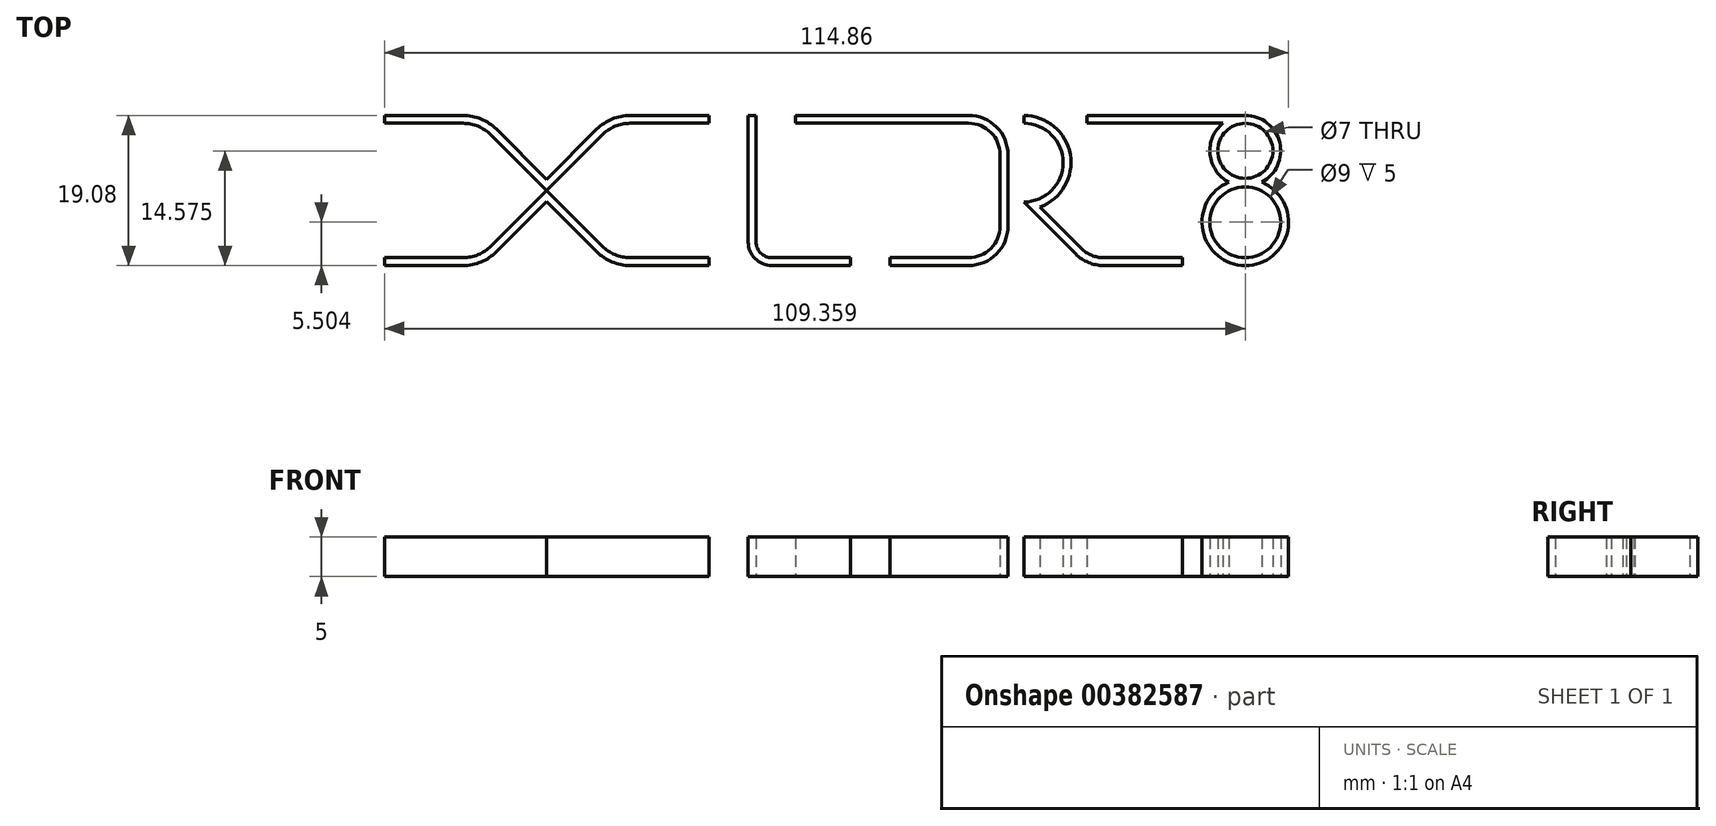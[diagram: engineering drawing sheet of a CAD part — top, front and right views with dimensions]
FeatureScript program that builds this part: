
annotation { "Feature Type Name" : "Feature", "Feature Type Description" : "" }
export const myFeature = defineFeature(function(context is Context, id is Id, definition is map)
    precondition{}
    {
        {
            var Q0;
            Q0=qCreatedBy(makeId("Top.planeOp"),FACE);
            var sketch = newSketch(context, id + "F0", { "sketchPlane" : qUnion([Q0])});
            skLineSegment(sketch, "E0", {"start": v(0, 0) * mm, "end": v(7.07, -7.07) * mm});
            skLineSegment(sketch, "E1", {"start": v(0, 0) * mm, "end": v(-7.07, 7.07) * mm});
            skLineSegment(sketch, "E2", {"start": v(0, 0) * mm, "end": v(7.07, 7.07) * mm});
            skLineSegment(sketch, "E3", {"start": v(0, 0) * mm, "end": v(-7.07, -7.07) * mm});
            skArc(sketch, "E4", {"start": v(10.6, 8.54) * mm, "mid": v(8.7, 8.15) * mm, "end": v(7.07, 7.07) * mm});
            skArc(sketch, "E5", {"start": v(-7.07, 7.07) * mm, "mid": v(-8.7, 8.15) * mm, "end": v(-10.6, 8.54) * mm});
            skArc(sketch, "E6", {"start": v(-10.6, -8.54) * mm, "mid": v(-8.7, -8.15) * mm, "end": v(-7.07, -7.07) * mm});
            skArc(sketch, "E7", {"start": v(7.07, -7.07) * mm, "mid": v(8.7, -8.15) * mm, "end": v(10.6, -8.54) * mm});
            skLineSegment(sketch, "E8", {"start": v(10.6, 8.54) * mm, "end": v(20.6, 8.54) * mm});
            skLineSegment(sketch, "E9", {"start": v(-10.6, 8.54) * mm, "end": v(-20.6, 8.54) * mm});
            skLineSegment(sketch, "E10", {"start": v(10.6, -8.54) * mm, "end": v(20.6, -8.54) * mm});
            skLineSegment(sketch, "E11", {"start": v(-10.6, -8.54) * mm, "end": v(-20.6, -8.54) * mm});
            skLineSegment(sketch, "E12.0", {"start": v(-10.6, 9.54) * mm, "end": v(-20.6, 9.54) * mm});
            skArc(sketch, "E12.1", {"start": v(-6.36, 7.78) * mm, "mid": v(-8.31, 9.08) * mm, "end": v(-10.6, 9.54) * mm});
            skLineSegment(sketch, "E12.2", {"start": v(10.6, 9.54) * mm, "end": v(20.6, 9.54) * mm});
            skArc(sketch, "E12.3", {"start": v(10.6, 9.54) * mm, "mid": v(8.31, 9.08) * mm, "end": v(6.36, 7.78) * mm});
            skLineSegment(sketch, "E12.4", {"start": v(0, 1.41) * mm, "end": v(6.36, 7.78) * mm});
            skLineSegment(sketch, "E12.5", {"start": v(0, 1.41) * mm, "end": v(-6.36, 7.78) * mm});
            skLineSegment(sketch, "E13.0", {"start": v(-10.6, -9.54) * mm, "end": v(-20.6, -9.54) * mm});
            skArc(sketch, "E13.1", {"start": v(-10.6, -9.54) * mm, "mid": v(-8.31, -9.08) * mm, "end": v(-6.36, -7.78) * mm});
            skLineSegment(sketch, "E13.2", {"start": v(10.6, -9.54) * mm, "end": v(20.6, -9.54) * mm});
            skArc(sketch, "E13.3", {"start": v(6.36, -7.78) * mm, "mid": v(8.31, -9.08) * mm, "end": v(10.6, -9.54) * mm});
            skLineSegment(sketch, "E13.4", {"start": v(0, -1.41) * mm, "end": v(6.36, -7.78) * mm});
            skLineSegment(sketch, "E13.5", {"start": v(0, -1.41) * mm, "end": v(-6.36, -7.78) * mm});
            skLineSegment(sketch, "E14", {"start": v(-20.6, 9.54) * mm, "end": v(-20.6, 8.54) * mm});
            skLineSegment(sketch, "E15", {"start": v(-20.6, -9.54) * mm, "end": v(-20.6, -8.54) * mm});
            skLineSegment(sketch, "E16", {"start": v(20.6, -8.54) * mm, "end": v(20.6, -9.54) * mm});
            skLineSegment(sketch, "E17", {"start": v(20.6, 9.54) * mm, "end": v(20.6, 8.54) * mm});
            skLineSegment(sketch, "E18", {"start": v(0, 0) * mm, "end": v(0, 0) * mm});
            skLineSegment(sketch, "E19", {"start": v(25.6, 9.54) * mm, "end": v(25.6, -6.54) * mm});
            skArc(sketch, "E20", {"start": v(25.6, -6.54) * mm, "mid": v(26.49, -8.66) * mm, "end": v(28.6, -9.54) * mm});
            skLineSegment(sketch, "E21", {"start": v(28.6, -9.54) * mm, "end": v(38.6, -9.54) * mm});
            skLineSegment(sketch, "E22.0", {"start": v(28.6, -8.54) * mm, "end": v(38.6, -8.54) * mm});
            skArc(sketch, "E22.1", {"start": v(26.6, -6.54) * mm, "mid": v(27.2, -7.95) * mm, "end": v(28.6, -8.54) * mm});
            skLineSegment(sketch, "E22.2", {"start": v(26.6, 9.54) * mm, "end": v(26.6, -6.54) * mm});
            skLineSegment(sketch, "E23", {"start": v(25.6, 9.54) * mm, "end": v(26.6, 9.54) * mm});
            skLineSegment(sketch, "E24", {"start": v(38.6, -8.54) * mm, "end": v(38.6, -9.54) * mm});
            skLineSegment(sketch, "E25", {"start": v(43.6, -9.54) * mm, "end": v(53.6, -9.54) * mm});
            skArc(sketch, "E26", {"start": v(53.6, -9.54) * mm, "mid": v(57.14, -8.07) * mm, "end": v(58.6, -4.54) * mm});
            skLineSegment(sketch, "E27", {"start": v(58.6, -4.54) * mm, "end": v(58.6, 4.54) * mm});
            skArc(sketch, "E28", {"start": v(58.6, 4.54) * mm, "mid": v(57.14, 8.07) * mm, "end": v(53.6, 9.54) * mm});
            skLineSegment(sketch, "E29", {"start": v(53.6, 9.54) * mm, "end": v(31.6, 9.54) * mm});
            skLineSegment(sketch, "E30.0", {"start": v(53.6, 8.54) * mm, "end": v(31.6, 8.54) * mm});
            skLineSegment(sketch, "E30.1", {"start": v(43.6, -8.54) * mm, "end": v(53.6, -8.54) * mm});
            skArc(sketch, "E30.2", {"start": v(53.6, -8.54) * mm, "mid": v(56.44, -7.36) * mm, "end": v(57.6, -4.54) * mm});
            skLineSegment(sketch, "E30.3", {"start": v(57.6, -4.54) * mm, "end": v(57.6, 4.54) * mm});
            skArc(sketch, "E30.4", {"start": v(57.6, 4.54) * mm, "mid": v(56.44, 7.36) * mm, "end": v(53.6, 8.54) * mm});
            skLineSegment(sketch, "E31", {"start": v(31.6, 8.54) * mm, "end": v(31.6, 9.54) * mm});
            skLineSegment(sketch, "E32", {"start": v(43.6, -8.54) * mm, "end": v(43.6, -9.54) * mm});
            skLineSegment(sketch, "E33", {"start": v(60.6, -1.46) * mm, "end": v(67.21, -8.07) * mm});
            skArc(sketch, "E34", {"start": v(67.21, -8.07) * mm, "mid": v(68.84, -9.15) * mm, "end": v(70.75, -9.54) * mm});
            skLineSegment(sketch, "E35", {"start": v(70.75, -9.54) * mm, "end": v(80.75, -9.54) * mm});
            skArc(sketch, "E36", {"start": v(60.6, -1.46) * mm, "mid": v(65.6, 3.54) * mm, "end": v(60.6, 8.54) * mm});
            skArc(sketch, "E37.0", {"start": v(62.66, -2.1) * mm, "mid": v(66.52, 4.58) * mm, "end": v(60.6, 9.54) * mm});
            skLineSegment(sketch, "E37.1", {"start": v(62.66, -2.1) * mm, "end": v(67.92, -7.36) * mm});
            skArc(sketch, "E37.2", {"start": v(67.92, -7.36) * mm, "mid": v(69.22, -8.23) * mm, "end": v(70.75, -8.54) * mm});
            skLineSegment(sketch, "E37.3", {"start": v(70.75, -8.54) * mm, "end": v(80.75, -8.54) * mm});
            skLineSegment(sketch, "E38", {"start": v(60.6, 9.54) * mm, "end": v(60.6, 8.54) * mm});
            skLineSegment(sketch, "E39", {"start": v(80.75, -8.54) * mm, "end": v(80.75, -9.54) * mm});
            skCircle(sketch, "E40", {"center": v(88.75, -4.04) * mm, "radius": 5.5 * mm});
            skCircle(sketch, "E41", {"center": v(88.75, 5.04) * mm, "radius": 4.5 * mm});
            skLineSegment(sketch, "E42", {"start": v(68.6, 9.54) * mm, "end": v(88.75, 9.54) * mm});
            skLineSegment(sketch, "E43.0", {"start": v(68.6, 8.54) * mm, "end": v(88.75, 8.54) * mm});
            skLineSegment(sketch, "E44", {"start": v(68.6, 9.54) * mm, "end": v(68.6, 8.54) * mm});
            skLineSegment(sketch, "E45", {"start": v(88.75, 9.54) * mm, "end": v(88.75, 8.54) * mm});
            skCircle(sketch, "E46.0", {"center": v(88.75, -4.04) * mm, "radius": 4.5 * mm});
            skCircle(sketch, "E47.0", {"center": v(88.75, 5.04) * mm, "radius": 3.5 * mm});
            skPoint(sketch, "E48", {"position": v(94.25, -4.04) * mm});
            skPoint(sketch, "E49", {"position": v(34.82, 0.5) * mm});
            skCircle(sketch, "E50", {"center": v(34.82, 0.5) * mm, "radius": 62.5 * mm});
            skCircle(sketch, "E51.0", {"center": v(34.82, 0.5) * mm, "radius": 65 * mm});
            skSolve(sketch);
        }
        {
            var Q0;
            {var subQ1=sQuery(id+"F0.wireOp",EDGE,"E4");Q0=makeQuery(id+"F0.imprint","IMPRINT",FACE,{"disambiguationData":[TD([[makeQuery(id+"F0.imprint","IMPRINT",EDGE,{"derivedFrom":subQ1}),-1.0]])]});}
            var Q1;
            {var subQ0=sQuery(id+"F0.wireOp",EDGE,"E6");Q1=makeQuery(id+"F0.imprint","IMPRINT",FACE,{"disambiguationData":[TD([[makeQuery(id+"F0.imprint","IMPRINT",EDGE,{"derivedFrom":subQ0}),-1.0]])]});}
            var Q2;
            {var subQ3=sQuery(id+"F0.wireOp",EDGE,"E18");Q2=makeQuery(id+"F0.imprint","IMPRINT",FACE,{"disambiguationData":[TD([[makeQuery(id+"F0.imprint","IMPRINT",EDGE,{"derivedFrom":subQ3}),-1.0]])]});}
            var Q3;
            {var subQ3=sQuery(id+"F0.wireOp",EDGE,"E18");Q3=makeQuery(id+"F0.imprint","IMPRINT",FACE,{"disambiguationData":[TD([[makeQuery(id+"F0.imprint","IMPRINT",EDGE,{"derivedFrom":subQ3}),1.0]])]});}
            var Q4;
            Q4=makeQuery(id+"F0.imprint","IMPRINT",FACE,{"disambiguationData":[TD([[makeQuery(id+"F0.imprint","IMPRINT",EDGE,{"derivedFrom":sQuery(id+"F0.wireOp",EDGE,"E19")}),1.0]])]});
            var Q5;
            Q5=makeQuery(id+"F0.imprint","IMPRINT",FACE,{"disambiguationData":[TD([[makeQuery(id+"F0.imprint","IMPRINT",EDGE,{"derivedFrom":sQuery(id+"F0.wireOp",EDGE,"E25")}),1.0]])]});
            var Q6;
            Q6=makeQuery(id+"F0.imprint","IMPRINT",FACE,{"disambiguationData":[TD([[makeQuery(id+"F0.imprint","IMPRINT",EDGE,{"derivedFrom":sQuery(id+"F0.wireOp",EDGE,"E33")}),1.0]])]});
            var Q7;
            {var subQ0=sQuery(id+"F0.wireOp",EDGE,"E42");Q7=makeQuery(id+"F0.imprint","IMPRINT",FACE,{"disambiguationData":[TD([[makeQuery(id+"F0.imprint","IMPRINT",EDGE,{"derivedFrom":subQ0}),-1.0]])]});}
            var Q8;
            {var subQ1=sQuery(id+"F0.wireOp",EDGE,"E45");Q8=makeQuery(id+"F0.imprint","IMPRINT",FACE,{"disambiguationData":[TD([[makeQuery(id+"F0.imprint","IMPRINT",EDGE,{"derivedFrom":subQ1}),1.0]])]});}
            var Q9;
            {var subQ0=sQuery(id+"F0.wireOp",EDGE,"E45");Q9=makeQuery(id+"F0.imprint","IMPRINT",FACE,{"disambiguationData":[TD([[makeQuery(id+"F0.imprint","IMPRINT",EDGE,{"derivedFrom":subQ0}),-1.0]])]});}
            var Q10;
            {var subQ0=sQuery(id+"F0.wireOp",EDGE,"E41");var subQ1=sQuery(id+"F0.wireOp",EDGE,"E40");var subQ2=makeQuery(id+"F0.imprint","INTERSECT",VERTEX,{"disambiguationData":[OD(0.0)],"derivedFrom":[subQ1,subQ0]});Q10=makeQuery(id+"F0.imprint","IMPRINT",FACE,{"disambiguationData":[TD([[makeQuery(id+"F0.imprint","IMPRINT",EDGE,{"disambiguationData":[TD([[subQ2,1.0]])],"derivedFrom":subQ1}),1.0]])]});}
            var Q11;
            Q11=makeQuery(id+"F0.imprint","IMPRINT",FACE,{"disambiguationData":[TD([[makeQuery(id+"F0.imprint","IMPRINT",EDGE,{"derivedFrom":sQuery(id+"F0.wireOp",EDGE,"E46.0")}),-1.0]])]});
            extrude(context, id + "F1", {"entities" : qUnion([Q0, Q1, Q2, Q3, Q4, Q5, Q6, Q7, Q8, Q9, Q10, Q11]), "offsetDistance" : 25 * mm, "depth" : 5 * mm});
        }
    });
